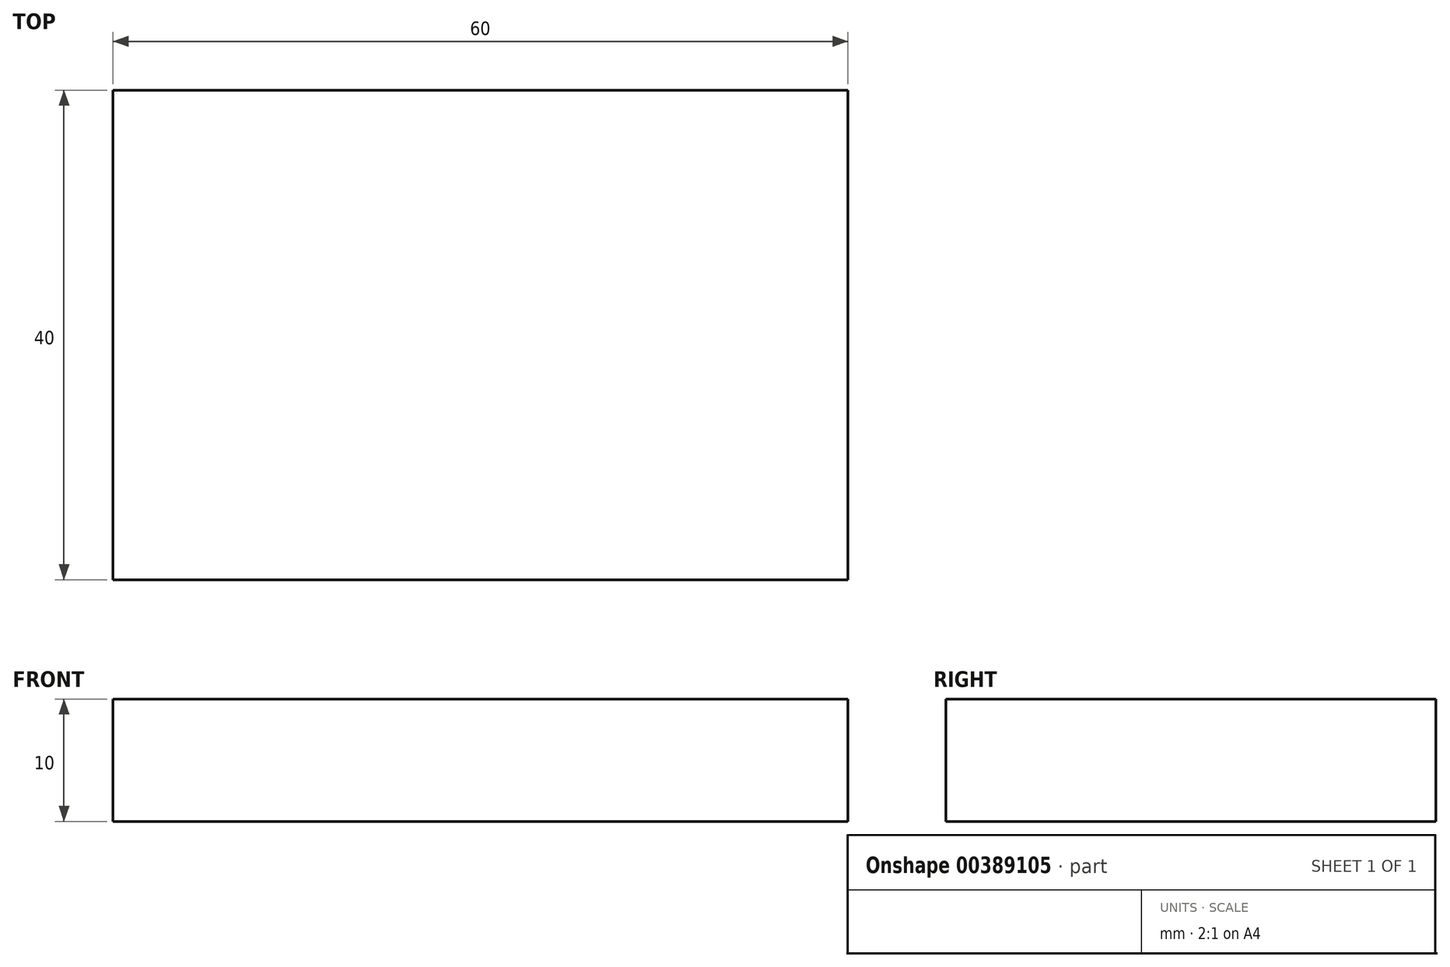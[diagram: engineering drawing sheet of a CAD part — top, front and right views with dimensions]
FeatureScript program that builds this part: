
annotation { "Feature Type Name" : "Feature", "Feature Type Description" : "" }
export const myFeature = defineFeature(function(context is Context, id is Id, definition is map)
    precondition{}
    {
        {
            var Q0;
            Q0=qCreatedBy(makeId("Top.planeOp"),FACE);
            var sketch = newSketch(context, id + "F0", { "sketchPlane" : qUnion([Q0])});
            skLineSegment(sketch, "E0.bottom", {"start": v(-30, 20) * mm, "end": v(30, 20) * mm});
            skLineSegment(sketch, "E0.top", {"start": v(-30, -20) * mm, "end": v(30, -20) * mm});
            skLineSegment(sketch, "E0.left", {"start": v(-30, 20) * mm, "end": v(-30, -20) * mm});
            skLineSegment(sketch, "E0.right", {"start": v(30, 20) * mm, "end": v(30, -20) * mm});
            skPoint(sketch, "E0.middle", {"position": v(0, 0) * mm});
            skSolve(sketch);
        }
        {
            var Q0;
            Q0=makeQuery(id+"F0.imprint","IMPRINT",FACE,{"disambiguationData":[TD([[makeQuery(id+"F0.imprint","IMPRINT",EDGE,{"derivedFrom":sQuery(id+"F0.wireOp",EDGE,"E0.bottom")}),-1.0]])]});
            extrude(context, id + "F1", {"entities" : qUnion([Q0]), "depth" : 10 * mm});
        }
    });
